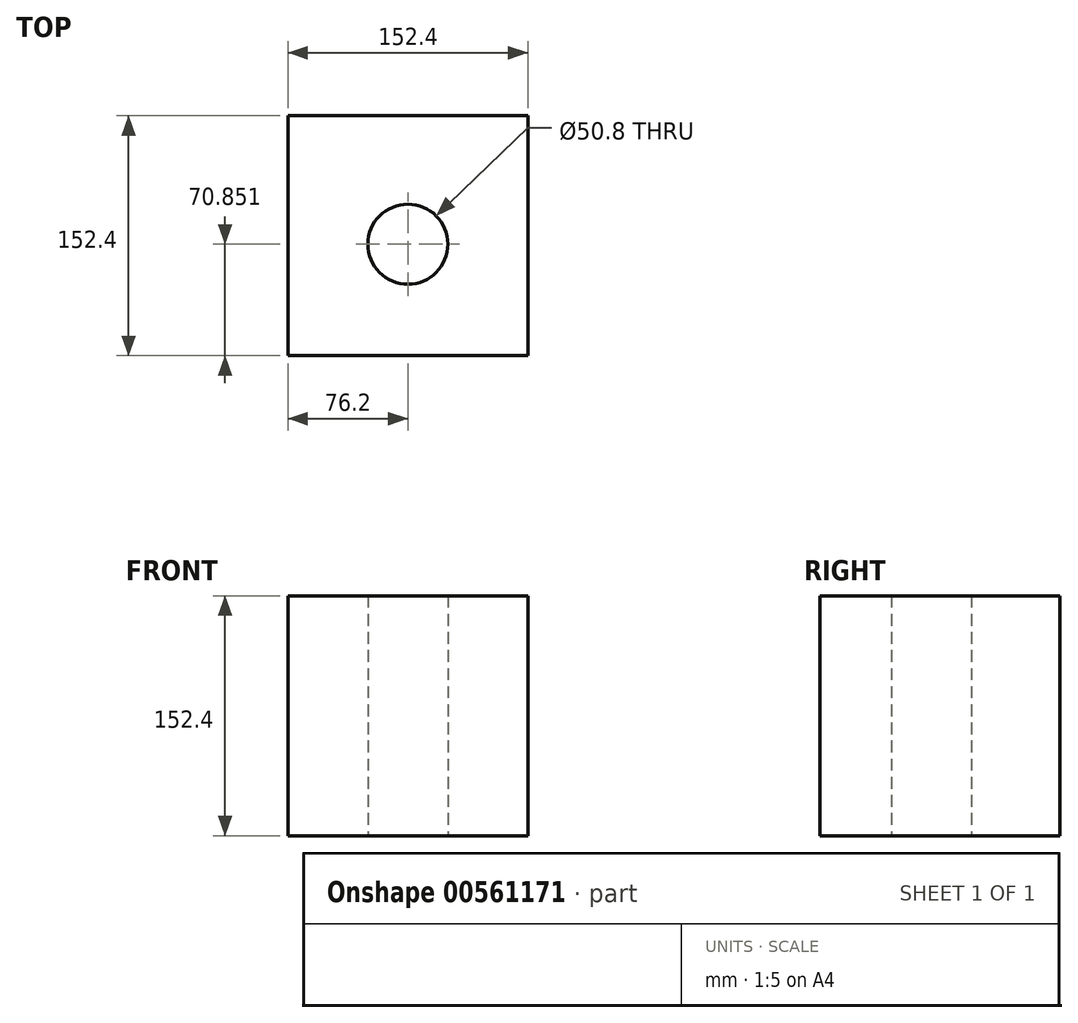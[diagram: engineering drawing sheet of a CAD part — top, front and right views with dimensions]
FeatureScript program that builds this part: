
annotation { "Feature Type Name" : "Feature", "Feature Type Description" : "" }
export const myFeature = defineFeature(function(context is Context, id is Id, definition is map)
    precondition{}
    {
        {
            var Q0;
            Q0=qCreatedBy(makeId("Top.planeOp"),FACE);
            var sketch = newSketch(context, id + "F0", { "sketchPlane" : qUnion([Q0])});
            skPoint(sketch, "E0.middle", {"position": v(0, 0) * mm});
            skLineSegment(sketch, "E1.bottom", {"start": v(76.2, 76.2) * mm, "end": v(-76.2, 76.2) * mm});
            skLineSegment(sketch, "E1.top", {"start": v(76.2, -76.2) * mm, "end": v(-76.2, -76.2) * mm});
            skLineSegment(sketch, "E1.left", {"start": v(76.2, 76.2) * mm, "end": v(76.2, -76.2) * mm});
            skLineSegment(sketch, "E1.right", {"start": v(-76.2, 76.2) * mm, "end": v(-76.2, -76.2) * mm});
            skSolve(sketch);
        }
        {
            var Q0;
            Q0=makeQuery(id+"F0.imprint","IMPRINT",FACE,{"disambiguationData":[TD([[makeQuery(id+"F0.imprint","IMPRINT",EDGE,{"derivedFrom":sQuery(id+"F0.wireOp",EDGE,"E1.bottom")}),1.0]])]});
            extrude(context, id + "F1", {"entities" : qUnion([Q0]), "depth" : 152.4 * mm, "offsetDistance" : 25.4 * mm});
        }
        {
            var Q0;
            Q0=makeQuery(id+"F1.opExtrude","CAP_FACE",FACE,{"disambiguationData":[OSD([sQuery(id+"F0.wireOp",EDGE,"E1.bottom"),sQuery(id+"F0.wireOp",EDGE,"E1.top"),sQuery(id+"F0.wireOp",EDGE,"E1.left"),sQuery(id+"F0.wireOp",EDGE,"E1.right")])],"isStart":true});
            var sketch = newSketch(context, id + "F2", { "sketchPlane" : qUnion([Q0])});
            skCircle(sketch, "E2", {"center": v(0, 5.35) * mm, "radius": 25.4 * mm});
            skSolve(sketch);
        }
        {
            var Q0;
            Q0=makeQuery(id+"F2.imprint","IMPRINT",FACE,{"disambiguationData":[TD([[makeQuery(id+"F2.imprint","IMPRINT",EDGE,{"derivedFrom":sQuery(id+"F2.wireOp",EDGE,"E2")}),1.0]])]});
            extrude(context, id + "F3", {"entities" : qUnion([Q0]), "operationType" : NewBodyOperationType.REMOVE, "endBound" : BoundingType.THROUGH_ALL, "oppositeDirection" : true, "depth" : 152.4 * mm, "offsetDistance" : 25.4 * mm});
        }
    });
